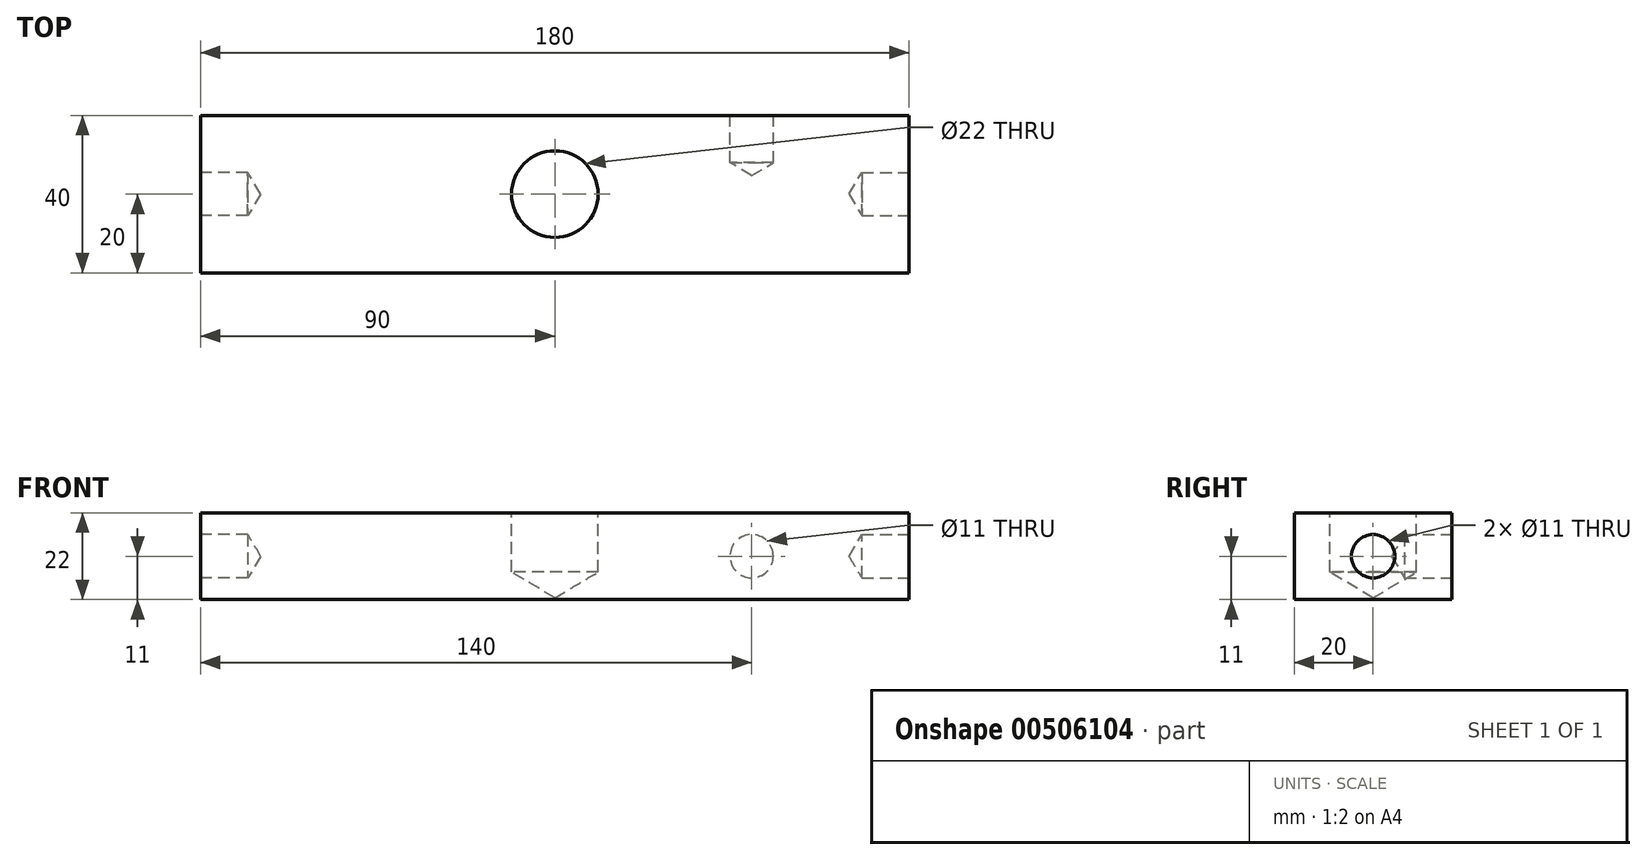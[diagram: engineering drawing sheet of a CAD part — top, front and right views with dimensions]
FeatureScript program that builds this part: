
annotation { "Feature Type Name" : "Feature", "Feature Type Description" : "" }
export const myFeature = defineFeature(function(context is Context, id is Id, definition is map)
    precondition{}
    {
        {
            var Q0;
            Q0=qCreatedBy(makeId("Top.planeOp"),FACE);
            var sketch = newSketch(context, id + "F0", { "sketchPlane" : qUnion([Q0])});
            skLineSegment(sketch, "E0.bottom", {"start": v(-90, 20) * mm, "end": v(90, 20) * mm});
            skLineSegment(sketch, "E0.top", {"start": v(-90, -20) * mm, "end": v(90, -20) * mm});
            skLineSegment(sketch, "E0.left", {"start": v(-90, 20) * mm, "end": v(-90, -20) * mm});
            skLineSegment(sketch, "E0.right", {"start": v(90, 20) * mm, "end": v(90, -20) * mm});
            skPoint(sketch, "E0.middle", {"position": v(0, 0) * mm});
            skSolve(sketch);
        }
        {
            var Q0;
            Q0 = qSketchRegion(id + "F0", true);
            extrude(context, id + "F1", {"entities" : qUnion([Q0]), "oppositeDirection" : true, "depth" : 22 * mm});
        }
        {
            var Q0;
            Q0=makeQuery(id+"F1.opExtrude","CAP_FACE",FACE,{"disambiguationData":[OSD([sQuery(id+"F0.wireOp",EDGE,"E0.bottom"),sQuery(id+"F0.wireOp",EDGE,"E0.top"),sQuery(id+"F0.wireOp",EDGE,"E0.left"),sQuery(id+"F0.wireOp",EDGE,"E0.right")])],"isStart":true});
            var sketch = newSketch(context, id + "F2", { "sketchPlane" : qUnion([Q0])});
            skCircle(sketch, "E1", {"center": v(0, 0) * mm, "radius": 3.56 * mm});
            skSolve(sketch);
        }
        {
            var Q0;
            Q0=sQuery(id+"F2.wireOp",VERTEX,"E1.center");
            var Q1;
            Q1=makeQuery(id+"F1.opExtrude","SWEPT_BODY",BODY,{"disambiguationData":[OSD([sQuery(id+"F0.wireOp",EDGE,"E0.bottom"),sQuery(id+"F0.wireOp",EDGE,"E0.top"),sQuery(id+"F0.wireOp",EDGE,"E0.left"),sQuery(id+"F0.wireOp",EDGE,"E0.right")])]});
            hole(context, id + "F3", {"style" : HoleStyle.SIMPLE, "endStyle" : HoleEndStyle.BLIND, "standardTappedOrClearance" : lookupTablePath({ "standard" : "ISO", "fit" : "Normal", "size" : "M20", "type" : "Clearance" }), "standardBlindInLast" : lookupTablePath({ "fit" : "Standard", "standard" : "ISO", "size" : "M20", "type" : "Clearance" }), "holeDiameter" : 22 * mm, "holeDepth" : 15 * mm, "isTappedThrough" : true, "tappedDepth" : 12 * mm, "tapClearance" : 3, "locations" : qUnion([Q0]), "scope" : qUnion([Q1])});
        }
        {
            var Q0;
            Q0=makeQuery(id+"F1.opExtrude","SWEPT_FACE",FACE,{"disambiguationData":[OSD([sQuery(id+"F0.wireOp",EDGE,"E0.left")])]});
            var sketch = newSketch(context, id + "F4", { "sketchPlane" : qUnion([Q0])});
            skLineSegment(sketch, "E2", {"start": v(-20, -22) * mm, "end": v(20, 0) * mm, "construction": true});
            skLineSegment(sketch, "E3", {"start": v(20, -22) * mm, "end": v(-20, 0) * mm, "construction": true});
            skCircle(sketch, "E4", {"center": v(0, -11) * mm, "radius": 3.8 * mm});
            skSolve(sketch);
        }
        {
            var Q0;
            Q0=sQuery(id+"F4.wireOp",VERTEX,"E4.center");
            var Q1;
            Q1=makeQuery(id+"F1.opExtrude","SWEPT_BODY",BODY,{"disambiguationData":[OSD([sQuery(id+"F0.wireOp",EDGE,"E0.bottom"),sQuery(id+"F0.wireOp",EDGE,"E0.top"),sQuery(id+"F0.wireOp",EDGE,"E0.left"),sQuery(id+"F0.wireOp",EDGE,"E0.right")])]});
            hole(context, id + "F5", {"style" : HoleStyle.SIMPLE, "endStyle" : HoleEndStyle.BLIND, "standardTappedOrClearance" : lookupTablePath({ "standard" : "ISO", "fit" : "Normal", "size" : "M10", "type" : "Clearance" }), "standardBlindInLast" : lookupTablePath({ "fit" : "Standard", "standard" : "ISO", "size" : "M10", "type" : "Clearance" }), "holeDiameter" : 11 * mm, "holeDepth" : 12 * mm, "isTappedThrough" : true, "tappedDepth" : 12 * mm, "tapClearance" : 3, "locations" : qUnion([Q0]), "scope" : qUnion([Q1])});
        }
        {
            var Q0;
            Q0=makeQuery(id+"F1.opExtrude","SWEPT_FACE",FACE,{"disambiguationData":[OSD([sQuery(id+"F0.wireOp",EDGE,"E0.right")])]});
            var sketch = newSketch(context, id + "F6", { "sketchPlane" : qUnion([Q0])});
            skLineSegment(sketch, "E5", {"start": v(-20, -22) * mm, "end": v(20, 0) * mm, "construction": true});
            skLineSegment(sketch, "E6", {"start": v(20, -22) * mm, "end": v(-20, 0) * mm, "construction": true});
            skCircle(sketch, "E7", {"center": v(0, -11) * mm, "radius": 3.07 * mm, "construction": true});
            skSolve(sketch);
        }
        {
            var Q0;
            Q0=sQuery(id+"F6.wireOp",VERTEX,"E7.center");
            var Q1;
            Q1=makeQuery(id+"F1.opExtrude","SWEPT_BODY",BODY,{"disambiguationData":[OSD([sQuery(id+"F0.wireOp",EDGE,"E0.bottom"),sQuery(id+"F0.wireOp",EDGE,"E0.top"),sQuery(id+"F0.wireOp",EDGE,"E0.left"),sQuery(id+"F0.wireOp",EDGE,"E0.right")])]});
            hole(context, id + "F7", {"style" : HoleStyle.SIMPLE, "endStyle" : HoleEndStyle.BLIND, "standardTappedOrClearance" : lookupTablePath({ "standard" : "ISO", "fit" : "Normal", "size" : "M10", "type" : "Clearance" }), "standardBlindInLast" : lookupTablePath({ "fit" : "Standard", "standard" : "ISO", "size" : "M10", "type" : "Clearance" }), "holeDiameter" : 11 * mm, "holeDepth" : 12 * mm, "isTappedThrough" : true, "tappedDepth" : 12 * mm, "tapClearance" : 3, "locations" : qUnion([Q0]), "scope" : qUnion([Q1])});
        }
        {
            var Q0;
            Q0=makeQuery(id+"F1.opExtrude","SWEPT_FACE",FACE,{"disambiguationData":[OSD([sQuery(id+"F0.wireOp",EDGE,"E0.bottom")])]});
            var sketch = newSketch(context, id + "F8", { "sketchPlane" : qUnion([Q0])});
            skLineSegment(sketch, "E8", {"start": v(-28.35, -11) * mm, "end": v(-105.11, -11) * mm, "construction": true});
            skLineSegment(sketch, "E9", {"start": v(-50, -40.93) * mm, "end": v(-50, 36.3) * mm, "construction": true});
            skCircle(sketch, "E10", {"center": v(-50, -11) * mm, "radius": 3.4 * mm});
            skSolve(sketch);
        }
        {
            var Q0;
            Q0=sQuery(id+"F8.wireOp",VERTEX,"E10.center");
            var Q1;
            Q1=makeQuery(id+"F1.opExtrude","SWEPT_BODY",BODY,{"disambiguationData":[OSD([sQuery(id+"F0.wireOp",EDGE,"E0.bottom"),sQuery(id+"F0.wireOp",EDGE,"E0.top"),sQuery(id+"F0.wireOp",EDGE,"E0.left"),sQuery(id+"F0.wireOp",EDGE,"E0.right")])]});
            hole(context, id + "F9", {"style" : HoleStyle.SIMPLE, "endStyle" : HoleEndStyle.BLIND, "standardTappedOrClearance" : lookupTablePath({ "standard" : "ISO", "fit" : "Normal", "size" : "M10", "type" : "Clearance" }), "standardBlindInLast" : lookupTablePath({ "fit" : "Standard", "standard" : "ISO", "size" : "M10", "type" : "Clearance" }), "holeDiameter" : 11 * mm, "holeDepth" : 12 * mm, "isTappedThrough" : true, "tappedDepth" : 12 * mm, "tapClearance" : 3, "locations" : qUnion([Q0]), "scope" : qUnion([Q1])});
        }
    });
